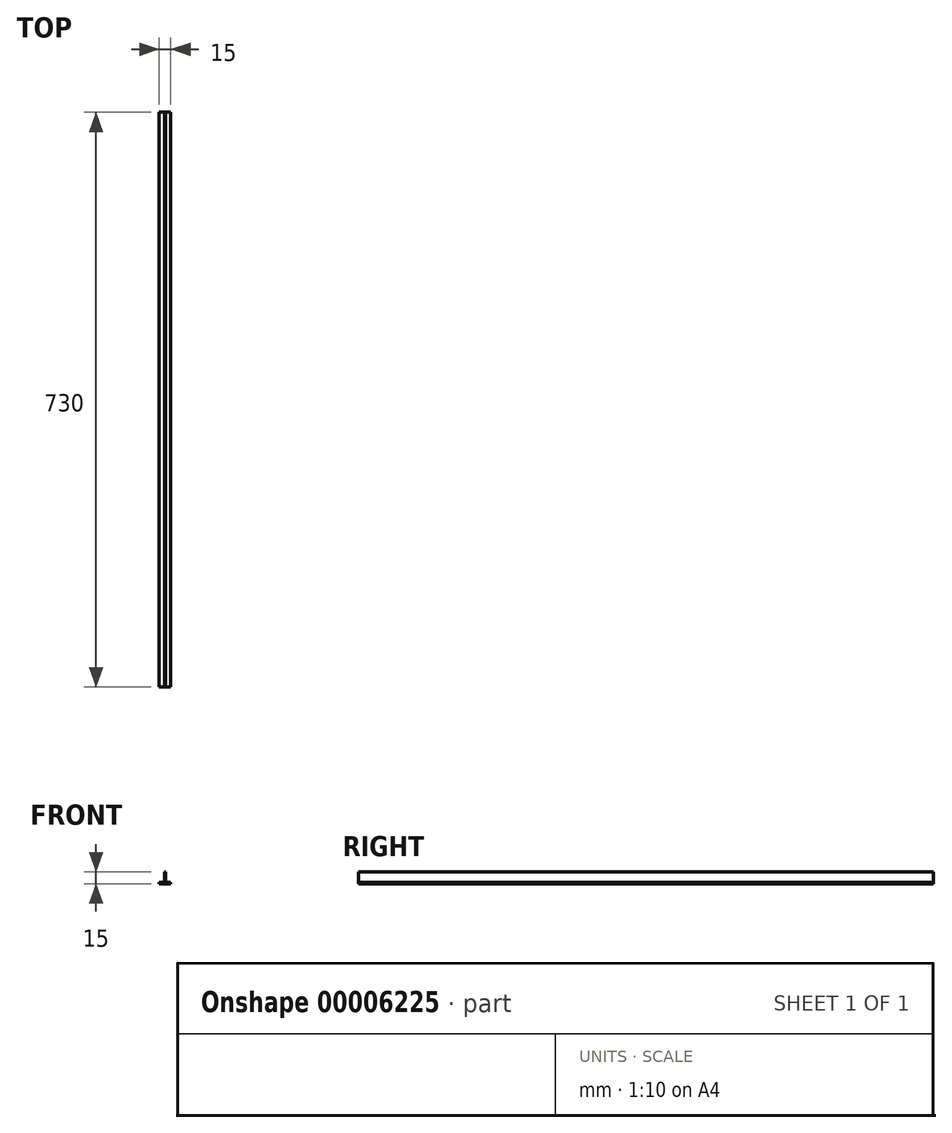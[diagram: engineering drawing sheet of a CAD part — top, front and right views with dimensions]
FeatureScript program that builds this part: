
annotation { "Feature Type Name" : "Feature", "Feature Type Description" : "" }
export const myFeature = defineFeature(function(context is Context, id is Id, definition is map)
    precondition{}
    {
        {
            var Q0;
            Q0=qCreatedBy(makeId("Front.planeOp"),FACE);
            var sketch = newSketch(context, id + "F0", { "sketchPlane" : qUnion([Q0])});
            skLineSegment(sketch, "E0.rect.bottom", {"start": v(7.5, 0.75) * mm, "end": v(0.75, 0.75) * mm});
            skLineSegment(sketch, "E0.rect.top", {"start": v(7.5, -0.75) * mm, "end": v(-7.5, -0.75) * mm});
            skLineSegment(sketch, "E0.rect.left", {"start": v(7.5, 0.75) * mm, "end": v(7.5, -0.75) * mm});
            skLineSegment(sketch, "E0.rect.right", {"start": v(-7.5, 0.75) * mm, "end": v(-7.5, -0.75) * mm});
            skPoint(sketch, "E0.rect.middle", {"position": v(0, 0) * mm});
            skLineSegment(sketch, "E1.rect.bottom", {"start": v(0.75, 14.25) * mm, "end": v(-0.75, 14.25) * mm});
            skLineSegment(sketch, "E1.rect.left", {"start": v(0.75, 14.25) * mm, "end": v(0.75, 0.75) * mm});
            skLineSegment(sketch, "E1.rect.right", {"start": v(-0.75, 14.25) * mm, "end": v(-0.75, 0.75) * mm});
            skPoint(sketch, "E1.rect.top.start.orphan", {"position": v(0.75, -14.25) * mm});
            skPoint(sketch, "E2.orphan", {"position": v(-0.75, -14.25) * mm});
            skLineSegment(sketch, "E3.trimOffspring", {"start": v(-0.75, 0.75) * mm, "end": v(-7.5, 0.75) * mm});
            skSolve(sketch);
        }
        {
            var Q0;
            Q0=qSketchRegion(id+"F0",true);
            extrude(context, id + "F1", {"entities" : qUnion([Q0]), "depth" : 730 * mm});
        }
    });
